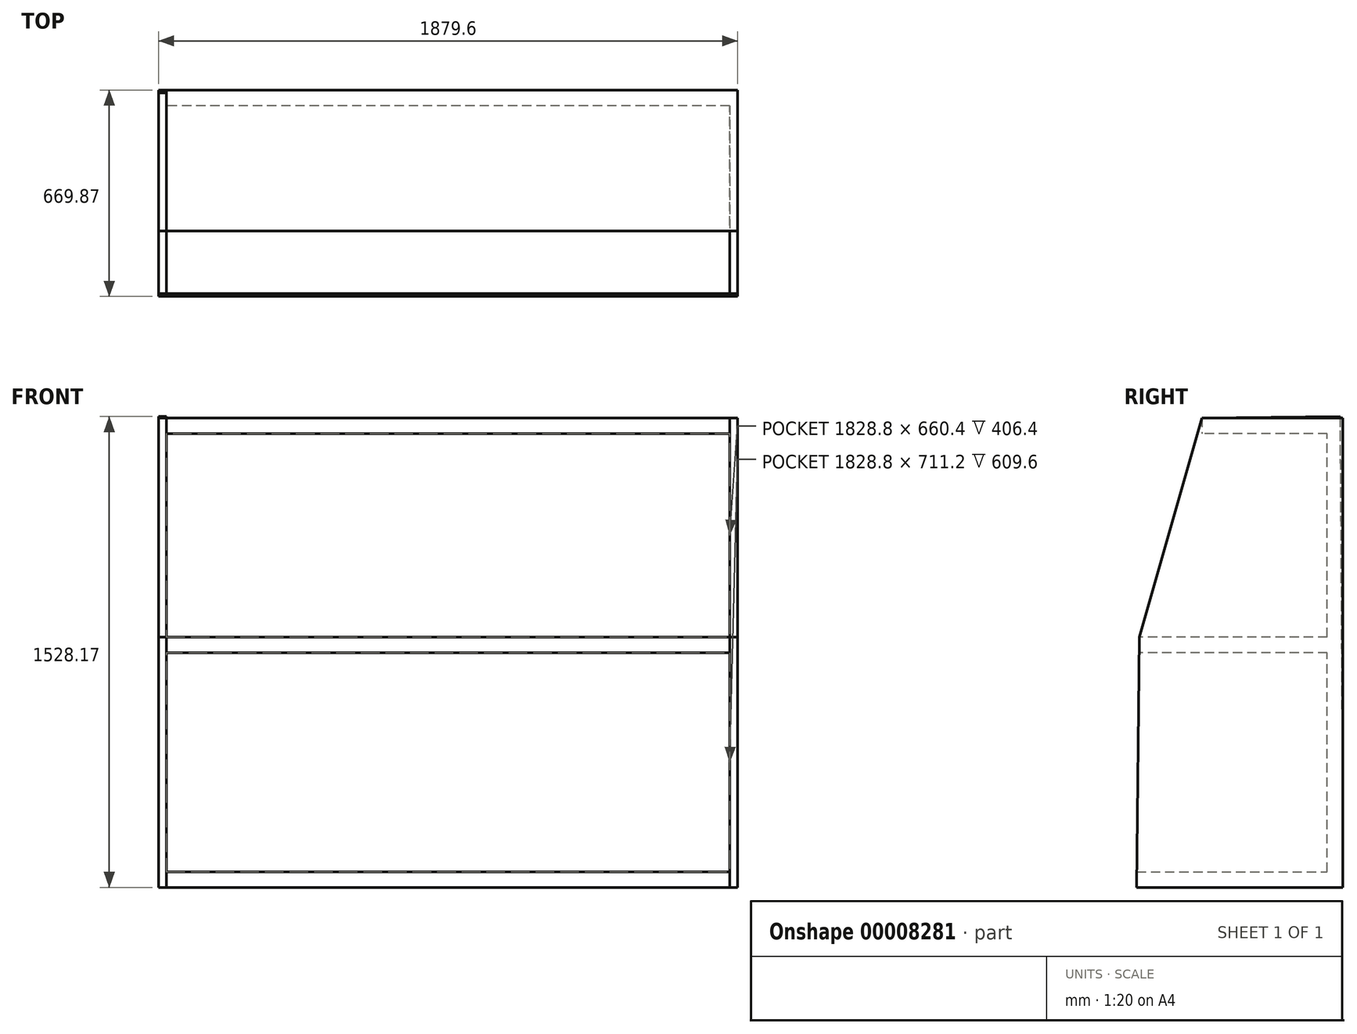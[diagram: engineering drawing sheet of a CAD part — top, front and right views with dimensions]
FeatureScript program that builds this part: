
annotation { "Feature Type Name" : "Feature", "Feature Type Description" : "" }
export const myFeature = defineFeature(function(context is Context, id is Id, definition is map)
    precondition{}
    {
        {
            var Q0;
            Q0=qCreatedBy(makeId("Right.planeOp"),FACE);
            var sketch = newSketch(context, id + "F0", { "sketchPlane" : qUnion([Q0])});
            skLineSegment(sketch, "E0.bottom", {"start": v(-540.05, -709.24) * mm, "end": v(79.02, -709.24) * mm});
            skLineSegment(sketch, "E0.top", {"start": v(-540.05, -658.44) * mm, "end": v(79.02, -658.44) * mm});
            skLineSegment(sketch, "E0.left", {"start": v(-540.05, -709.24) * mm, "end": v(-540.05, -658.44) * mm});
            skLineSegment(sketch, "E0.right", {"start": v(79.02, -709.24) * mm, "end": v(79.02, -658.44) * mm});
            skLineSegment(sketch, "E1.bottom", {"start": v(129.82, -709.24) * mm, "end": v(79.02, -709.24) * mm});
            skLineSegment(sketch, "E1.top", {"start": v(129.82, 814.76) * mm, "end": v(79.02, 814.76) * mm});
            skLineSegment(sketch, "E1.left", {"start": v(79.02, -709.24) * mm, "end": v(79.02, 814.76) * mm});
            skLineSegment(sketch, "E1.right", {"start": v(129.82, -709.24) * mm, "end": v(129.82, 814.76) * mm});
            skLineSegment(sketch, "E2.bottom", {"start": v(79.02, 103.56) * mm, "end": v(-530.58, 103.56) * mm});
            skLineSegment(sketch, "E2.top", {"start": v(79.02, 52.76) * mm, "end": v(-530.58, 52.76) * mm});
            skLineSegment(sketch, "E2.left", {"start": v(79.02, 103.56) * mm, "end": v(79.02, 52.76) * mm});
            skLineSegment(sketch, "E2.right", {"start": v(-530.58, 103.56) * mm, "end": v(-530.58, 52.76) * mm});
            skLineSegment(sketch, "E3.bottom", {"start": v(129.82, 814.76) * mm, "end": v(-327.38, 814.76) * mm});
            skLineSegment(sketch, "E3.top", {"start": v(129.82, 763.96) * mm, "end": v(-327.38, 763.96) * mm});
            skLineSegment(sketch, "E3.left", {"start": v(129.82, 814.76) * mm, "end": v(129.82, 763.96) * mm});
            skLineSegment(sketch, "E3.right", {"start": v(-327.38, 814.76) * mm, "end": v(-327.38, 763.96) * mm});
            skSolve(sketch);
        }
        {
            var Q0;
            Q0 = qSketchRegion(id + "F0", true);
            extrude(context, id + "F1", {"entities" : qUnion([Q0]), "depth" : 1828.8 * mm});
        }
        {
            var Q0;
            Q0=qCreatedBy(makeId("Right.planeOp"),FACE);
            var sketch = newSketch(context, id + "F2", { "sketchPlane" : qUnion([Q0])});
            skPoint(sketch, "E4", {"position": v(120.24, 818.93) * mm});
            skPoint(sketch, "E5", {"position": v(-327.38, 814.76) * mm});
            skPoint(sketch, "E6", {"position": v(-530.58, 103.56) * mm});
            skPoint(sketch, "E7", {"position": v(-530.58, 52.76) * mm});
            skPoint(sketch, "E8", {"position": v(-540.05, -709.24) * mm});
            skPoint(sketch, "E9", {"position": v(129.82, -709.24) * mm});
            skLineSegment(sketch, "E10", {"start": v(120.24, 818.93) * mm, "end": v(-327.38, 814.76) * mm});
            skLineSegment(sketch, "E11", {"start": v(-530.58, 103.56) * mm, "end": v(-327.38, 814.76) * mm});
            skLineSegment(sketch, "E12", {"start": v(120.24, 818.93) * mm, "end": v(129.82, -709.24) * mm});
            skLineSegment(sketch, "E13", {"start": v(-540.05, -709.24) * mm, "end": v(-530.58, 103.56) * mm});
            skLineSegment(sketch, "E14", {"start": v(129.82, -709.24) * mm, "end": v(-540.05, -709.24) * mm});
            skSolve(sketch);
        }
        {
            var Q0;
            Q0 = qSketchRegion(id + "F2", true);
            extrude(context, id + "F3", {"entities" : qUnion([Q0]), "operationType" : NewBodyOperationType.ADD, "oppositeDirection" : true, "depth" : 25.4 * mm});
        }
        {
            var Q0;
            Q0=makeQuery(id+"F1.opExtrude","CAP_FACE",FACE,{"disambiguationData":[OSD([sQuery(id+"F0.wireOp",EDGE,"E0.bottom"),sQuery(id+"F0.wireOp",EDGE,"E0.top"),sQuery(id+"F0.wireOp",EDGE,"E0.left"),sQuery(id+"F0.wireOp",EDGE,"E1.bottom"),sQuery(id+"F0.wireOp",EDGE,"E1.left"),sQuery(id+"F0.wireOp",EDGE,"E1.right"),sQuery(id+"F0.wireOp",EDGE,"E2.bottom"),sQuery(id+"F0.wireOp",EDGE,"E2.top"),sQuery(id+"F0.wireOp",EDGE,"E2.right"),sQuery(id+"F0.wireOp",EDGE,"E3.bottom"),sQuery(id+"F0.wireOp",EDGE,"E3.top"),sQuery(id+"F0.wireOp",EDGE,"E3.left"),sQuery(id+"F0.wireOp",EDGE,"E3.right")])],"isStart":false});
            var sketch = newSketch(context, id + "F4", { "sketchPlane" : qUnion([Q0])});
            skLineSegment(sketch, "E15", {"start": v(-327.38, 814.76) * mm, "end": v(-530.58, 103.56) * mm});
            skLineSegment(sketch, "E16", {"start": v(-530.58, 103.56) * mm, "end": v(-540.05, -709.24) * mm});
            skLineSegment(sketch, "E17", {"start": v(-540.05, -709.24) * mm, "end": v(129.82, -709.24) * mm});
            skLineSegment(sketch, "E18", {"start": v(129.82, -709.24) * mm, "end": v(129.82, 814.76) * mm});
            skLineSegment(sketch, "E19", {"start": v(129.82, 814.76) * mm, "end": v(-327.38, 814.76) * mm});
            skSolve(sketch);
        }
        {
            var Q0;
            Q0 = qSketchRegion(id + "F4", true);
            extrude(context, id + "F5", {"entities" : qUnion([Q0]), "operationType" : NewBodyOperationType.ADD, "depth" : 25.4 * mm});
        }
    });
